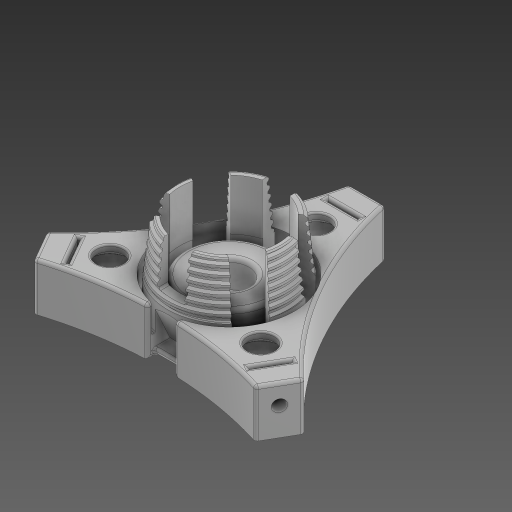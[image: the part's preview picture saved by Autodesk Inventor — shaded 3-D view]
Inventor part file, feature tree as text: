
AUTODESK INVENTOR PART (.ipt)
format: ipt  version: 2024 (Build 280153000, 153)  size: 1,769,472 bytes
history: native  units: mm
features: sketch x18, extrude x13, fillet x10, chamfer x4, hole x3, pattern_circular x3, draft x2, helix x2, plane x2, projected_geometry x2
ambient origin geometry x8: Origin, YZ Plane, XZ Plane, XY Plane, X Axis, Y Axis, Z Axis, Center Point
bodies: Solid1 (feature_tree)
feature tree (59):
  extrude  "Extrusion1"  Depth=29.5mm
  draft  "FaceDraft1"
  sketch  "Sketch2"  dims[d7=6.806784mm d8=0.55605mm]
  helix  "Coil1"  [1 undecoded]
  helix  "Coil2"  [1 undecoded]
  extrude  "Extrusion2"  Depth=0.55605mm
  extrude  "Extrusion3"  TaperAngle=0.0deg  [1 undecoded]
  fillet  "Fillet1"  [1 undecoded]
  chamfer  "Chamfer1"  Distance=0.3mm Angle=45.0deg
  plane  "Work Plane1"
  extrude  "Extrusion4"  TaperAngle=0.0deg  [1 undecoded]
  extrude  "Extrusion8"  Depth=60.0mm TaperAngle=360.0deg
  hole  "Hole2"  [1 undecoded]
  sketch  "Sketch13"  dims[d58=6.0mm d65=60.0mm d67=360.0deg]
  extrude  "Extrusion11"  Depth=10.0mm TaperAngle=0.0deg
  hole  "Bearing Hole"  [1 undecoded]
  pattern_circular  "Circular Pattern4"  Count=3 Angle=360.0deg
  extrude  "Extrusion13"  Depth=7.0mm TaperAngle=0.0deg
  sketch  "Sketch20"  dims[d126=6.804mm d127=6.0mm d128=9.979mm d129=8.89mm d130=90.0deg d131=8.0mm d132=20.594885mm d133=22.0mm d134=30.0mm d135=360.0deg]
  extrude  "Extrusion14"  Depth=1.55mm TaperAngle=45.0deg
  sketch  "Sketch18"  dims[d124=34.0mm]
  fillet  "Fillet9"  Radius=0.24mm
  chamfer  "Chamfer4"  [1 undecoded]
  chamfer  "Chamfer5"  Distance=2.0mm
  fillet  "Fillet11"  Radius=34.767mm
  draft  "FaceDraft2"
  fillet  "Fillet13"  Radius=9.0mm
  extrude  "Extrusion15"  TaperAngle=30.0deg  [1 undecoded]
  hole  "Hole5"  [1 undecoded]
  pattern_circular  "Circular Pattern5"  [2 undecoded]
  plane  "Work Plane4"
  extrude  "Extrusion16"  Depth=0.75mm TaperAngle=360.0deg
  fillet  "Fillet14"  Radius=16.0mm
  fillet  "Fillet16"  [1 undecoded]
  extrude  "Extrusion17"  Depth=0.75mm
  extrude  "Extrusion19"  Depth=0.75mm
  fillet  "Fillet17"  Radius=25.0mm
  fillet  "Fillet18"  Radius=22.0mm
  fillet  "Fillet19"  Radius=31.0mm
  extrude  "Extrusion20"  Depth=0.75mm TaperAngle=0.0deg
  fillet  "Fillet20"  Radius=32.8mm
  chamfer  "Chamfer6"  Distance=9.0mm
  pattern_circular  "Circular Pattern6"  [2 undecoded]
  sketch  "Sketch1"  dims[d0=24.7mm d1=29.5mm d2=12.875mm d3=0.0mm d4=1.047198mm]
  projected_geometry  "Projected Loop1"
  sketch  "Sketch3"  dims[d9=6.806784mm]
  sketch  "Sketch4"  dims[d10=2.0mm d11=10.0mm d12=70.0mm d13=-1.047198mm d14=90.0deg d15=90.0deg d16=0.0mm d17=0.0mm d18=0.6mm]
  sketch  "Sketch5"  dims[d19=2.0mm d20=10.0mm d21=10.0mm d22=1.047198mm d23=90.0deg d24=90.0deg d25=0.0mm d26=0.0mm d27=0.0mm d28=0.0mm d29=0.0mm d30=0.0mm]
  sketch  "Sketch10"  dims[d31=0.6mm d32=0.3mm d33=2.0mm d34=45.0deg]
  sketch  "Sketch11"  dims[d36=-2.0mm d42=0.0mm d43=0.0mm]
  sketch  "Sketch15"  dims[d91=33.0mm d92=12.0mm d93=0.0mm]
  sketch  "Sketch17"  dims[d94=5.3mm d95=6.0mm d96=10.0mm d97=7.0mm d98=90.0deg d99=8.0mm d100=20.594885mm d122=10.0mm d123=0.0mm]
  sketch  "Sketch21"  dims[d146=11.34464mm d147=7.0mm d148=0.0mm]
  sketch  "Sketch22"  dims[d150=1.0mm d151=1.55mm d152=2.0mm d153=45.0deg]
  sketch  "Sketch25"  dims[d154=0.5mm d155=2.0mm d156=45.0deg d158=0.24mm]
  sketch  "Sketch26"  dims[d160=1.25mm d161=0.0mm d162=0.0mm]
  sketch  "Sketch28"  dims[d163=30.0deg]
  sketch  "Sketch29"  dims[d164=0.5mm d165=2.0mm d166=34.767mm d167=9.0mm d168=30.0deg d169=7.0mm d170=0.0mm d171=3.0mm d172=6.0mm d173=9.779mm d174=7.62mm d175=90.0deg d176=7.0mm d177=0.0mm d178=5.0mm d179=30.0mm d180=360.0deg d182=16.0mm d183=0.0mm d184=0.0mm d185=0.75mm d187=0.4mm d188=25.0mm d189=22.0mm d190=31.0mm d191=7.0mm d192=0.0mm d193=32.8mm d208=9.0mm d209=0.0mm d210=1.0mm d211=0.25mm d212=0.5mm d213=7.0mm d214=60.0mm d216=360.0deg d218=8.0mm d219=6.0mm d220=0.6mm d221=0.3mm d222=0.0mm d223=0.0mm d224=0.75mm d225=0.75mm d226=2.0mm d227=45.0deg d228=30.0mm d229=360.0deg]
  projected_geometry  "Project Cut Edges3"
note: 15 required parameter values undecoded (feature->parameter linkage not recoverable at this tier; creation-order binding heuristic only, values carry confidence <= 0.55)
